# Revit family: 08805202
name_source: partatom
category: Plumbing Fixtures
revit_build: Autodesk Revit 2018 (Build: 20170223_1515(x64)
units: mm (PartAtom-declared; Revit-internal decimal feet)

## family parameters
Always vertical = Yes
Cut with Voids When Loaded = No
OmniClass Number = 23.45.55.00
OmniClass Title = Sanitary Faucets, Wastes
Part Type = Normal
Room Calculation Point = No
Round Connector Dimension = Use Diameter
Shared = No
Work Plane-Based = No

## types (1)
- 08805202 Washbasin faucet
    2D/3D/BIM Files URL = http://static.hansa.com
    3D View = https://static.hansa.com
    Additional Features = Safety lock against scalding 38°C (36°-44°)
    Advanced Features = Inner body made of DZR brass;Waterways without nickel coating;Thermal disinfection without cartridge readjustment
    Aerator = Laminar stream
    Ambience photo = http://static.hansa.com
    Approval DVGW = NW-6509CR0103
    AssetType = Fixed
    BIMObjectName = 08805202
    Backflow Prevention EN1717 = AA
    BodyMaterial = Brass
    Brand = HANSA
    Catalog Drawing URL = http://static.hansa.com
    Category = Health & Care
    CloseOffRating = 0
    Color = Chrome
    Connection = Eccentric coupling(s);Cover plate(s);with integrated shut-off valve(s);Silencer(s);Cover plate triple sealed
    Connection Size = G1/2
    Dimension Drawing URL = http://static.hansa.com
    DurationUnit = Year
    EAN Number = 4057304013409
    EN Standard = EN 1111
    ETIM Class Number = EC011328 Washbasin mixing tap
    FDV Document URL = http://www.hansa.com
    FaucetMainMaterial = Brass
    Features = Thermostatic
    Finish = Polished
    Flow Drawing URL = http://static.hansa.com
    Flow Rate At 300kPa = 0.2 L/s
    FlowCoefficient = 0
    Group = Washbasin faucet
    HWFU = 0
    IfcExportAs = IfcValveType
    IfcExportType = FAUCET
    Installation Type = Wall mounted
    Installation Width = CC150± 10 mm
    Installation and Maintenance Guide URL = http://static.hansa.com
    Interactive AR View URL = https://static.hansa.com
    Lever Handle = Temperature control handle;Flow control handle;Long shape;Eco feature for water flow
    Lifestyle photo = http://static.hansa.com
    Manufacturer = HANSA
    ManufacturerName = HANSA
    ManufacturerURL = http://www.hansa.com
    Market = International;Germany;Austria;Switzerland;Belgium;Netherlands;France;Czech Republic;Slovakia;Hungary;Romania;Italy;Spain;Greece;Portugal;Australia
    Material = Brass
    Max. Hot Water Supply = 80 °C
    Mechanical Parts = Ceramic head part for flow control;Thermostatic cartridge for automatic temperature control;Non-return valve(s);Litter filter(s)
    Mobile Product Information URL = http://mpi.hansa.com
    Model = 08805202 Washbasin faucet
    ModelReference = 08805202
    NBSDescription = Water supply fittings for wash basins and troughs
    NBSReference = 45-35-70/371
    Name = 08805202 Washbasin faucet
    Name_en = 08805202 Washbasin faucet
    Noise Class = I (ISO 3822)
    NominalDepth = 296 mm
    NominalHeight = 120 mm
    NominalWidth = 289 mm
    Product Code = 08805202
    Product Family = HANSACLINICA Safety+
    Product Image URL = http://static.hansa.com
    Product URL = http://static.hansa.com
    Revision = 3
    Sales Package dimensions (LxWxH) = 407 x 265 x 119
    Shape = Sculptured
    Size = 290x295x120 mm
    Spare-Part Information URL = http://static.hansa.com
    Spout Projection = 285 mm
    Spout Swivel Range = 120° (60°/0°)
    Spout Type = Swivel spout;Lockable in the middle position;Swivel range limiting option;Profile construction
    Surface treatment = Chrome
    Technical DataSheet URL = http://www.hansa.com
    Temperature = THERMO COOL
    Temperature Adjustments = The housing of the fittings conducts minimal heat
    UNSPSC Class Number = 30181700 Faucets or taps
    URL DVGW = http://static.hansa.com
    URL Declaration of Conformity = http://static.hansa.com
    URL REACH = http://static.hansa.com
    Uniclass2 = Pr_40_30_96_99
    Uniclass2015Description = Washbasin thermostatic water supply sets
    Uniclass2015Reference = Pr_40_20_87_99
    Version = 3
    VersionDate = 01/07/2022
    Warranty Information URL = http://warranty.hansa.com
    WarrantyDescription = http://warranty.hansa.com
    WarrantyDurationUnit = Year
    Working Pressure = 100 - 1000 kPa
    WorkingPressure = 100 - 1000 kPa

## geometry (parser evidence)
native form markers: Sweep x5
no freeform markers — native parametric forms only
